# Revit family: PRE050013-FR
name_source: partatom
category: Accessoire de canalisation
revit_build: Autodesk Revit 2017 (Build: 20160225_1515(x64)
units: mm (PartAtom-declared; Revit-internal decimal feet)

## family parameters
Basée sur le plan de construction = Non
Cote de connecteur circulaire = Utiliser le diamètre
Couper avec des vides une fois chargée = Non
Partagée = Non
Toujours verticalement = Oui
Type d'élément = Normal

## types (1)
- 52041 PRESTO ROBINET ELECTRONIQUE MURAL PRESTORIZON PILE TOUT INTEGRE
    Adresse = 7, RUE RACINE - 92542 MONTROUGE CEDEX FRANCE
    Debit = 3 l/min par limiteur de débit intégré

Aérateur anti-tartre haute qualité

Dispositif anti-coup de bélier
    Description = Robinet électronique mural pour lavabo, avec électronique intégrée de type Presto Prestorizon réf 52041 ou techniquement équivalent. Débit 3L/min par limiteur de débit intégré. Alimentation pile lithium 9V  et électrovanne ½’’intégrées dans le corps du robinet. Diamètre du tube 45 mm.Système antiblocage interdisant l’écoulement continu de plus de 30 secondes. Rinçage automatique de 45 secondes, toutes les 24h après la dernière utilisation.
    Diamètre Nominal = 15 mm  [stored 0.0492126 ft]
    Fabricant = LES ROBINETS PRESTO S.A.
    Finition = Corps en laiton avec finition chromée
    Flux = 0.1 L/s
    Fonction = Pression d'utilisation recommandée :
- 1 à 5 bars

Débit :
- 3 l/mn par régulateur de débit intégré
- Aérateur anti-tartre haute qualité

Alimentation hydraulique :
- G 1/2'' (15x21)
- 1 électrovanne 1/2'' intégrée dans le corps du robinet

Alimentation électrique :
- Pile lithium 9 volts intégrée dans le corps du robinet

Matière et couleur de finition :
- Corps en laiton avec finition chromée
- Longueur de bec : 220 mm
- Saillie : 205 mm
- Diamètre du tube: 45 mm
- Diamètre de la rosace: 60 mm

Résistance thermique :
- Ce robinet résiste à une température maximale de 65°C

Sécurité :
- Fermeture automatique de l'électrovanne en cas d'écoulement > à 30s
- Ecoulement automatique de 45 secondes, 24 heures après la dernière utilisation

Installation:
- Murale

Livré avec :
- 1 Ecrou de fixation, 1 joint et une rondelle
- 1 rosace de fixation murale
- 1 Autocollant de signalisation et 1 notice d'installation

Normes / Agréments :
- ACS et CE

ATTENTION :
- Pour un bon fonctionnement, éviter d'installer le produit face à des surfaces réfléchissantes
- Ne pas utiliser de bonde métallique
- Positionner le produit à 30 cm minimum du fond de la vasque
- Le produit est livré avec les paramètres communiqués sur la fiche technique . Il est possible de modifier les paramètres à l'aide de la télécommande (réf. 90071)
    Garantie = 3
    HC = 30 mm  [stored 0.0984252 ft]
    Hauteur = 60 mm  [stored 0.19685 ft]
    Largeur = 60 mm  [stored 0.19685 ft]
    Lien CCTP = http://www.prestodatashare.com
    Lien fiche produit = http://www.prestodatashare.com
    Lien notice d'utilisation = http://www.prestodatashare.com
    Matériau = Laiton poli chromé
    Modèle = 52041 PRESTO ROBINET ELECTRONIQUE MURAL PRESTORIZON PILE TOUT INTEGRE
    Perte de charge = 0.0 Pa
    Polantis code = PRE050013-FR
    Pression = 1 à 5 bars
    Profondeur = 220 mm  [stored 0.721785 ft]
    Raccordement = G ½’’ (15x21)
    Reference = 52041
    URL = http://www.prestodatashare.com
    URL Fabricant = http://www.prestodatashare.com
    Variantes = 52041

note: [stored X ft] marks values corroborated as IEEE doubles in the binary element streams (Revit-internal decimal feet)
